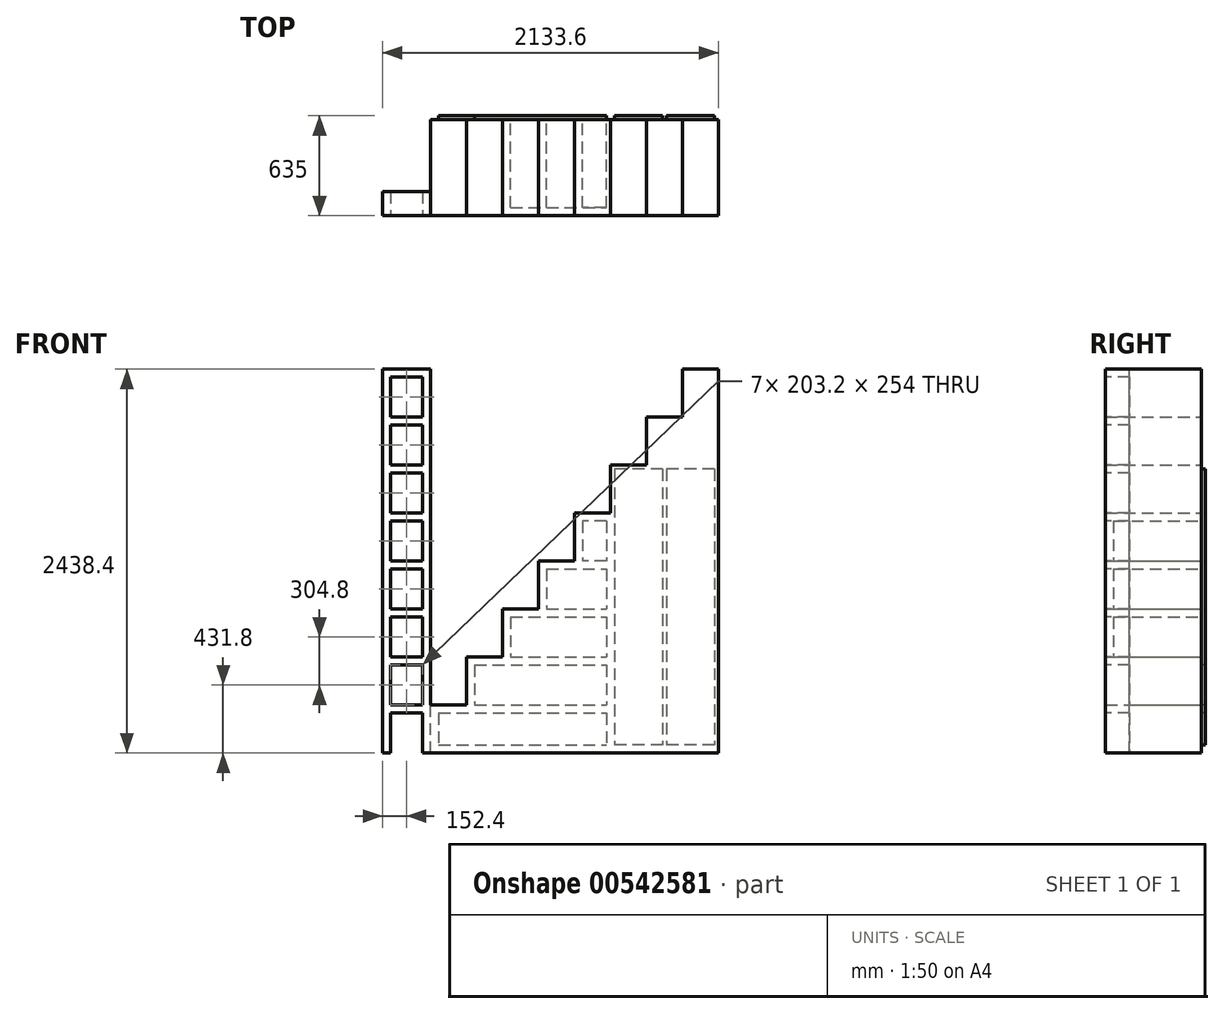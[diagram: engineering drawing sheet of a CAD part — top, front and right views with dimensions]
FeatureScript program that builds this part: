
annotation { "Feature Type Name" : "Feature", "Feature Type Description" : "" }
export const myFeature = defineFeature(function(context is Context, id is Id, definition is map)
    precondition{}
    {
        {
            var Q0;
            Q0=qCreatedBy(makeId("Front.planeOp"),FACE);
            var sketch = newSketch(context, id + "F0", { "sketchPlane" : qUnion([Q0])});
            skLineSegment(sketch, "E0.bottom", {"start": v(-1828.8, 0) * mm, "end": v(0, 0) * mm});
            skLineSegment(sketch, "E0.top", {"start": v(-1828.8, 304.8) * mm, "end": v(0, 304.8) * mm});
            skLineSegment(sketch, "E0.left", {"start": v(-1828.8, 0) * mm, "end": v(-1828.8, 304.8) * mm});
            skLineSegment(sketch, "E0.right", {"start": v(0, 0) * mm, "end": v(0, 304.8) * mm});
            skLineSegment(sketch, "E1.bottom", {"start": v(-1600.2, 304.8) * mm, "end": v(0, 304.8) * mm});
            skLineSegment(sketch, "E1.top", {"start": v(-1600.2, 609.6) * mm, "end": v(0, 609.6) * mm});
            skLineSegment(sketch, "E1.left", {"start": v(-1600.2, 304.8) * mm, "end": v(-1600.2, 609.6) * mm});
            skLineSegment(sketch, "E1.right", {"start": v(0, 304.8) * mm, "end": v(0, 609.6) * mm});
            skLineSegment(sketch, "E2.bottom", {"start": v(-1371.6, 609.6) * mm, "end": v(0, 609.6) * mm});
            skLineSegment(sketch, "E2.top", {"start": v(-1371.6, 914.4) * mm, "end": v(0, 914.4) * mm});
            skLineSegment(sketch, "E2.left", {"start": v(-1371.6, 609.6) * mm, "end": v(-1371.6, 914.4) * mm});
            skLineSegment(sketch, "E2.right", {"start": v(0, 609.6) * mm, "end": v(0, 914.4) * mm});
            skLineSegment(sketch, "E3.bottom", {"start": v(0, 914.4) * mm, "end": v(-1143, 914.4) * mm});
            skLineSegment(sketch, "E3.top", {"start": v(0, 1219.2) * mm, "end": v(-1143, 1219.2) * mm});
            skLineSegment(sketch, "E3.left", {"start": v(0, 914.4) * mm, "end": v(0, 1219.2) * mm});
            skLineSegment(sketch, "E3.right", {"start": v(-1143, 914.4) * mm, "end": v(-1143, 1219.2) * mm});
            skLineSegment(sketch, "E4.bottom", {"start": v(0, 1219.2) * mm, "end": v(-914.4, 1219.2) * mm});
            skLineSegment(sketch, "E4.top", {"start": v(0, 1524) * mm, "end": v(-914.4, 1524) * mm});
            skLineSegment(sketch, "E4.left", {"start": v(0, 1219.2) * mm, "end": v(0, 1524) * mm});
            skLineSegment(sketch, "E4.right", {"start": v(-914.4, 1219.2) * mm, "end": v(-914.4, 1524) * mm});
            skLineSegment(sketch, "E5.bottom", {"start": v(0, 1524) * mm, "end": v(-685.8, 1524) * mm});
            skLineSegment(sketch, "E5.top", {"start": v(0, 1828.8) * mm, "end": v(-685.8, 1828.8) * mm});
            skLineSegment(sketch, "E5.left", {"start": v(0, 1524) * mm, "end": v(0, 1828.8) * mm});
            skLineSegment(sketch, "E5.right", {"start": v(-685.8, 1524) * mm, "end": v(-685.8, 1828.8) * mm});
            skLineSegment(sketch, "E6.bottom", {"start": v(0, 1828.8) * mm, "end": v(-457.2, 1828.8) * mm});
            skLineSegment(sketch, "E6.top", {"start": v(0, 2133.6) * mm, "end": v(-457.2, 2133.6) * mm});
            skLineSegment(sketch, "E6.left", {"start": v(0, 1828.8) * mm, "end": v(0, 2133.6) * mm});
            skLineSegment(sketch, "E6.right", {"start": v(-457.2, 1828.8) * mm, "end": v(-457.2, 2133.6) * mm});
            skLineSegment(sketch, "E7.bottom", {"start": v(0, 2133.6) * mm, "end": v(-228.6, 2133.6) * mm});
            skLineSegment(sketch, "E7.top", {"start": v(0, 2438.4) * mm, "end": v(-228.6, 2438.4) * mm});
            skLineSegment(sketch, "E7.left", {"start": v(0, 2133.6) * mm, "end": v(0, 2438.4) * mm});
            skLineSegment(sketch, "E7.right", {"start": v(-228.6, 2133.6) * mm, "end": v(-228.6, 2438.4) * mm});
            skSolve(sketch);
        }
        {
            var Q0;
            Q0 = qSketchRegion(id + "F0", true);
            extrude(context, id + "F1", {"entities" : qUnion([Q0]), "depth" : 609.6 * mm, "offsetDistance" : 30.48 * mm});
        }
        {
            var Q0;
            Q0=makeQuery(id+"F1.opExtrude","CAP_FACE",FACE,{"disambiguationData":[OSD([sQuery(id+"F0.wireOp",EDGE,"E0.bottom"),sQuery(id+"F0.wireOp",EDGE,"E0.top"),sQuery(id+"F0.wireOp",EDGE,"E0.left"),sQuery(id+"F0.wireOp",EDGE,"E0.right"),sQuery(id+"F0.wireOp",EDGE,"E1.top"),sQuery(id+"F0.wireOp",EDGE,"E1.left"),sQuery(id+"F0.wireOp",EDGE,"E1.right"),sQuery(id+"F0.wireOp",EDGE,"E2.top"),sQuery(id+"F0.wireOp",EDGE,"E2.left"),sQuery(id+"F0.wireOp",EDGE,"E2.right"),sQuery(id+"F0.wireOp",EDGE,"E3.top"),sQuery(id+"F0.wireOp",EDGE,"E3.left"),sQuery(id+"F0.wireOp",EDGE,"E3.right"),sQuery(id+"F0.wireOp",EDGE,"E4.top"),sQuery(id+"F0.wireOp",EDGE,"E4.left"),sQuery(id+"F0.wireOp",EDGE,"E4.right"),sQuery(id+"F0.wireOp",EDGE,"E5.top"),sQuery(id+"F0.wireOp",EDGE,"E5.left"),sQuery(id+"F0.wireOp",EDGE,"E5.right"),sQuery(id+"F0.wireOp",EDGE,"E6.top"),sQuery(id+"F0.wireOp",EDGE,"E6.left"),sQuery(id+"F0.wireOp",EDGE,"E6.right"),sQuery(id+"F0.wireOp",EDGE,"E7.top"),sQuery(id+"F0.wireOp",EDGE,"E7.left"),sQuery(id+"F0.wireOp",EDGE,"E7.right")])],"isStart":false});
            var sketch = newSketch(context, id + "F2", { "sketchPlane" : qUnion([Q0])});
            skLineSegment(sketch, "E8.bottom", {"start": v(-1828.8, 0) * mm, "end": v(-1879.6, 0) * mm});
            skLineSegment(sketch, "E8.top", {"start": v(-1828.8, 2438.4) * mm, "end": v(-2133.6, 2438.4) * mm});
            skLineSegment(sketch, "E8.left", {"start": v(-1828.8, 0) * mm, "end": v(-1828.8, 2438.4) * mm});
            skLineSegment(sketch, "E8.right", {"start": v(-2133.6, 0) * mm, "end": v(-2133.6, 2438.4) * mm});
            skLineSegment(sketch, "E9.bottom", {"start": v(-2082.8, 2438.4) * mm, "end": v(-1879.6, 2438.4) * mm});
            skLineSegment(sketch, "E9.left", {"start": v(-2082.8, 2438.4) * mm, "end": v(-2082.8, 0) * mm});
            skLineSegment(sketch, "E9.right", {"start": v(-1879.6, 2438.4) * mm, "end": v(-1879.6, 0) * mm});
            skLineSegment(sketch, "E10", {"start": v(-1879.6, 304.8) * mm, "end": v(-2082.8, 304.8) * mm});
            skLineSegment(sketch, "E11", {"start": v(-1879.6, 609.6) * mm, "end": v(-2082.8, 609.6) * mm});
            skLineSegment(sketch, "E12", {"start": v(-1879.6, 914.4) * mm, "end": v(-2082.8, 914.4) * mm});
            skLineSegment(sketch, "E13", {"start": v(-1879.6, 863.6) * mm, "end": v(-2082.8, 863.6) * mm});
            skLineSegment(sketch, "E14", {"start": v(-2082.8, 558.8) * mm, "end": v(-1879.6, 558.8) * mm});
            skLineSegment(sketch, "E15", {"start": v(-2082.8, 254) * mm, "end": v(-1879.6, 254) * mm});
            skLineSegment(sketch, "E16.bottom", {"start": v(-2082.8, 1168.4) * mm, "end": v(-1879.6, 1168.4) * mm});
            skLineSegment(sketch, "E16.top", {"start": v(-2082.8, 1219.2) * mm, "end": v(-1879.6, 1219.2) * mm});
            skLineSegment(sketch, "E16.left", {"start": v(-2082.8, 1168.4) * mm, "end": v(-2082.8, 1219.2) * mm});
            skLineSegment(sketch, "E16.right", {"start": v(-1879.6, 1168.4) * mm, "end": v(-1879.6, 1219.2) * mm});
            skLineSegment(sketch, "E17.bottom", {"start": v(-1879.6, 1524) * mm, "end": v(-2082.8, 1524) * mm});
            skLineSegment(sketch, "E17.top", {"start": v(-1879.6, 1473.2) * mm, "end": v(-2082.8, 1473.2) * mm});
            skLineSegment(sketch, "E17.left", {"start": v(-1879.6, 1524) * mm, "end": v(-1879.6, 1473.2) * mm});
            skLineSegment(sketch, "E17.right", {"start": v(-2082.8, 1524) * mm, "end": v(-2082.8, 1473.2) * mm});
            skLineSegment(sketch, "E18.bottom", {"start": v(-1879.6, 1828.8) * mm, "end": v(-2082.8, 1828.8) * mm});
            skLineSegment(sketch, "E18.top", {"start": v(-1879.6, 1778) * mm, "end": v(-2082.8, 1778) * mm});
            skLineSegment(sketch, "E18.left", {"start": v(-1879.6, 1828.8) * mm, "end": v(-1879.6, 1778) * mm});
            skLineSegment(sketch, "E18.right", {"start": v(-2082.8, 1828.8) * mm, "end": v(-2082.8, 1778) * mm});
            skLineSegment(sketch, "E19.bottom", {"start": v(-1879.6, 2133.6) * mm, "end": v(-2082.8, 2133.6) * mm});
            skLineSegment(sketch, "E19.top", {"start": v(-1879.6, 2082.8) * mm, "end": v(-2082.8, 2082.8) * mm});
            skLineSegment(sketch, "E19.left", {"start": v(-1879.6, 2133.6) * mm, "end": v(-1879.6, 2082.8) * mm});
            skLineSegment(sketch, "E19.right", {"start": v(-2082.8, 2133.6) * mm, "end": v(-2082.8, 2082.8) * mm});
            skLineSegment(sketch, "E20.top", {"start": v(-1879.6, 2387.6) * mm, "end": v(-2082.8, 2387.6) * mm});
            skLineSegment(sketch, "E20.left", {"start": v(-1879.6, 2387.6) * mm, "end": v(-1879.6, 2340.42) * mm});
            skLineSegment(sketch, "E20.right", {"start": v(-2082.8, 2387.6) * mm, "end": v(-2082.8, 2340.42) * mm});
            skLineSegment(sketch, "E21.trimOffspring", {"start": v(-2082.8, 0) * mm, "end": v(-2133.6, 0) * mm});
            skSolve(sketch);
        }
        {
            var Q0;
            Q0 = qSketchRegion(id + "F2", true);
            var Q1;
            Q1=makeQuery(id+"F2.imprint","IMPRINT",FACE,{"disambiguationData":[TD([[makeQuery(id+"F2.imprint","IMPRINT",EDGE,{"derivedFrom":sQuery(id+"F2.wireOp",EDGE,"E19.bottom")}),1.0]])]});
            var Q2;
            Q2=makeQuery(id+"F2.imprint","IMPRINT",FACE,{"disambiguationData":[TD([[makeQuery(id+"F2.imprint","IMPRINT",EDGE,{"derivedFrom":sQuery(id+"F2.wireOp",EDGE,"E18.bottom")}),1.0]])]});
            var Q3;
            Q3=makeQuery(id+"F2.imprint","IMPRINT",FACE,{"disambiguationData":[TD([[makeQuery(id+"F2.imprint","IMPRINT",EDGE,{"derivedFrom":sQuery(id+"F2.wireOp",EDGE,"E17.bottom")}),1.0]])]});
            var Q4;
            Q4=makeQuery(id+"F2.imprint","IMPRINT",FACE,{"disambiguationData":[TD([[makeQuery(id+"F2.imprint","IMPRINT",EDGE,{"derivedFrom":sQuery(id+"F2.wireOp",EDGE,"E16.bottom")}),1.0]])]});
            var Q5;
            {var subQ0=sQuery(id+"F2.wireOp",EDGE,"E12");Q5=makeQuery(id+"F2.imprint","IMPRINT",FACE,{"disambiguationData":[TD([[makeQuery(id+"F2.imprint","IMPRINT",EDGE,{"derivedFrom":subQ0}),1.0]])]});}
            var Q6;
            {var subQ0=sQuery(id+"F2.wireOp",EDGE,"E11");Q6=makeQuery(id+"F2.imprint","IMPRINT",FACE,{"disambiguationData":[TD([[makeQuery(id+"F2.imprint","IMPRINT",EDGE,{"derivedFrom":subQ0}),1.0]])]});}
            extrude(context, id + "F3", {"entities" : qUnion([Q0, Q1, Q2, Q3, Q4, Q5, Q6]), "operationType" : NewBodyOperationType.ADD, "oppositeDirection" : true, "depth" : 152.4 * mm, "offsetDistance" : 25.4 * mm});
        }
        {
            var Q0;
            Q0=makeQuery(id+"F1.opExtrude","CAP_FACE",FACE,{"disambiguationData":[OSD([sQuery(id+"F0.wireOp",EDGE,"E0.bottom"),sQuery(id+"F0.wireOp",EDGE,"E0.top"),sQuery(id+"F0.wireOp",EDGE,"E0.left"),sQuery(id+"F0.wireOp",EDGE,"E0.right"),sQuery(id+"F0.wireOp",EDGE,"E1.top"),sQuery(id+"F0.wireOp",EDGE,"E1.left"),sQuery(id+"F0.wireOp",EDGE,"E1.right"),sQuery(id+"F0.wireOp",EDGE,"E2.top"),sQuery(id+"F0.wireOp",EDGE,"E2.left"),sQuery(id+"F0.wireOp",EDGE,"E2.right"),sQuery(id+"F0.wireOp",EDGE,"E3.top"),sQuery(id+"F0.wireOp",EDGE,"E3.left"),sQuery(id+"F0.wireOp",EDGE,"E3.right"),sQuery(id+"F0.wireOp",EDGE,"E4.top"),sQuery(id+"F0.wireOp",EDGE,"E4.left"),sQuery(id+"F0.wireOp",EDGE,"E4.right"),sQuery(id+"F0.wireOp",EDGE,"E5.top"),sQuery(id+"F0.wireOp",EDGE,"E5.left"),sQuery(id+"F0.wireOp",EDGE,"E5.right"),sQuery(id+"F0.wireOp",EDGE,"E6.top"),sQuery(id+"F0.wireOp",EDGE,"E6.left"),sQuery(id+"F0.wireOp",EDGE,"E6.right"),sQuery(id+"F0.wireOp",EDGE,"E7.top"),sQuery(id+"F0.wireOp",EDGE,"E7.left"),sQuery(id+"F0.wireOp",EDGE,"E7.right")])],"isStart":true});
            var sketch = newSketch(context, id + "F4", { "sketchPlane" : qUnion([Q0])});
            skLineSegment(sketch, "E22", {"start": v(0, 0) * mm, "end": v(1828.8, 0) * mm, "construction": true});
            skLineSegment(sketch, "E23", {"start": v(1828.8, 0) * mm, "end": v(1828.8, 304.8) * mm, "construction": true});
            skLineSegment(sketch, "E24", {"start": v(1828.8, 304.8) * mm, "end": v(1600.2, 304.8) * mm, "construction": true});
            skLineSegment(sketch, "E25", {"start": v(1600.2, 304.8) * mm, "end": v(1600.2, 609.6) * mm, "construction": true});
            skLineSegment(sketch, "E26", {"start": v(1600.2, 609.6) * mm, "end": v(1371.6, 609.6) * mm, "construction": true});
            skLineSegment(sketch, "E27", {"start": v(1371.6, 609.6) * mm, "end": v(1371.6, 914.4) * mm, "construction": true});
            skLineSegment(sketch, "E28", {"start": v(1371.6, 914.4) * mm, "end": v(1143, 914.4) * mm, "construction": true});
            skLineSegment(sketch, "E29", {"start": v(1143, 914.4) * mm, "end": v(1143, 1219.2) * mm, "construction": true});
            skLineSegment(sketch, "E30", {"start": v(1143, 1219.2) * mm, "end": v(914.4, 1219.2) * mm, "construction": true});
            skLineSegment(sketch, "E31", {"start": v(914.4, 1219.2) * mm, "end": v(914.4, 1524) * mm, "construction": true});
            skLineSegment(sketch, "E32", {"start": v(914.4, 1524) * mm, "end": v(685.8, 1524) * mm, "construction": true});
            skLineSegment(sketch, "E33", {"start": v(685.8, 1524) * mm, "end": v(685.8, 1828.8) * mm, "construction": true});
            skLineSegment(sketch, "E34", {"start": v(685.8, 1828.8) * mm, "end": v(457.2, 1828.8) * mm, "construction": true});
            skLineSegment(sketch, "E35", {"start": v(457.2, 1828.8) * mm, "end": v(457.2, 2133.6) * mm, "construction": true});
            skLineSegment(sketch, "E36", {"start": v(457.2, 2133.6) * mm, "end": v(228.6, 2133.6) * mm, "construction": true});
            skLineSegment(sketch, "E37", {"start": v(228.6, 2133.6) * mm, "end": v(228.6, 2438.4) * mm, "construction": true});
            skLineSegment(sketch, "E38", {"start": v(228.6, 2438.4) * mm, "end": v(0, 2438.4) * mm, "construction": true});
            skLineSegment(sketch, "E39", {"start": v(0, 2438.4) * mm, "end": v(0, 0) * mm, "construction": true});
            skLineSegment(sketch, "E40.bottom", {"start": v(25.4, 1803.4) * mm, "end": v(660.4, 1803.4) * mm});
            skLineSegment(sketch, "E40.top", {"start": v(25.4, 50.8) * mm, "end": v(660.4, 50.8) * mm});
            skLineSegment(sketch, "E40.left", {"start": v(25.4, 1803.4) * mm, "end": v(25.4, 50.8) * mm});
            skLineSegment(sketch, "E40.right", {"start": v(660.4, 1803.4) * mm, "end": v(660.4, 50.8) * mm});
            skLineSegment(sketch, "E41.bottom", {"start": v(711.2, 1473.2) * mm, "end": v(863.6, 1473.2) * mm});
            skLineSegment(sketch, "E41.top", {"start": v(711.2, 1219.2) * mm, "end": v(863.6, 1219.2) * mm});
            skLineSegment(sketch, "E41.left", {"start": v(711.2, 1473.2) * mm, "end": v(711.2, 1219.2) * mm});
            skLineSegment(sketch, "E41.right", {"start": v(863.6, 1473.2) * mm, "end": v(863.6, 1219.2) * mm});
            skLineSegment(sketch, "E42.bottom", {"start": v(1092.2, 1168.4) * mm, "end": v(711.2, 1168.4) * mm});
            skLineSegment(sketch, "E42.top", {"start": v(1092.2, 914.4) * mm, "end": v(711.2, 914.4) * mm});
            skLineSegment(sketch, "E42.left", {"start": v(1092.2, 1168.4) * mm, "end": v(1092.2, 914.4) * mm});
            skLineSegment(sketch, "E42.right", {"start": v(711.2, 1168.4) * mm, "end": v(711.2, 914.4) * mm});
            skLineSegment(sketch, "E43.bottom", {"start": v(1320.8, 863.6) * mm, "end": v(711.2, 863.6) * mm});
            skLineSegment(sketch, "E43.top", {"start": v(1320.8, 609.6) * mm, "end": v(711.2, 609.6) * mm});
            skLineSegment(sketch, "E43.left", {"start": v(1320.8, 863.6) * mm, "end": v(1320.8, 609.6) * mm});
            skLineSegment(sketch, "E43.right", {"start": v(711.2, 863.6) * mm, "end": v(711.2, 609.6) * mm});
            skLineSegment(sketch, "E44.bottom", {"start": v(1549.4, 558.8) * mm, "end": v(711.2, 558.8) * mm});
            skLineSegment(sketch, "E44.top", {"start": v(1549.4, 304.8) * mm, "end": v(711.2, 304.8) * mm});
            skLineSegment(sketch, "E44.left", {"start": v(1549.4, 558.8) * mm, "end": v(1549.4, 304.8) * mm});
            skLineSegment(sketch, "E44.right", {"start": v(711.2, 558.8) * mm, "end": v(711.2, 304.8) * mm});
            skLineSegment(sketch, "E45.bottom", {"start": v(1778, 254) * mm, "end": v(711.2, 254) * mm});
            skLineSegment(sketch, "E45.top", {"start": v(1778, 50.8) * mm, "end": v(711.2, 50.8) * mm});
            skLineSegment(sketch, "E45.left", {"start": v(1778, 254) * mm, "end": v(1778, 50.8) * mm});
            skLineSegment(sketch, "E45.right", {"start": v(711.2, 254) * mm, "end": v(711.2, 50.8) * mm});
            skLineSegment(sketch, "E46.bottom", {"start": v(330.2, 1803.4) * mm, "end": v(355.6, 1803.4) * mm});
            skLineSegment(sketch, "E46.top", {"start": v(330.2, 50.8) * mm, "end": v(355.6, 50.8) * mm});
            skLineSegment(sketch, "E46.left", {"start": v(330.2, 1803.4) * mm, "end": v(330.2, 50.8) * mm});
            skLineSegment(sketch, "E46.right", {"start": v(355.6, 1803.4) * mm, "end": v(355.6, 50.8) * mm});
            skSolve(sketch);
        }
        {
            var Q0;
            Q0=makeQuery(id+"F4.imprint","IMPRINT",FACE,{"disambiguationData":[TD([[makeQuery(id+"F4.imprint","IMPRINT",EDGE,{"derivedFrom":sQuery(id+"F4.wireOp",EDGE,"E41.bottom")}),-1.0]])]});
            var Q1;
            Q1=makeQuery(id+"F4.imprint","IMPRINT",FACE,{"disambiguationData":[TD([[makeQuery(id+"F4.imprint","IMPRINT",EDGE,{"derivedFrom":sQuery(id+"F4.wireOp",EDGE,"E42.bottom")}),1.0]])]});
            var Q2;
            Q2=makeQuery(id+"F4.imprint","IMPRINT",FACE,{"disambiguationData":[TD([[makeQuery(id+"F4.imprint","IMPRINT",EDGE,{"derivedFrom":sQuery(id+"F4.wireOp",EDGE,"E43.bottom")}),1.0]])]});
            extrude(context, id + "F5", {"entities" : qUnion([Q0, Q1, Q2]), "operationType" : NewBodyOperationType.REMOVE, "oppositeDirection" : true, "depth" : 558.8 * mm, "offsetDistance" : 25.4 * mm});
        }
        {
            var Q0;
            {var subQ0=sQuery(id+"F4.wireOp",EDGE,"E40.left");Q0=makeQuery(id+"F4.imprint","IMPRINT",FACE,{"disambiguationData":[TD([[makeQuery(id+"F4.imprint","IMPRINT",EDGE,{"derivedFrom":subQ0}),1.0]])]});}
            var Q1;
            {var subQ0=sQuery(id+"F4.wireOp",EDGE,"E40.right");Q1=makeQuery(id+"F4.imprint","IMPRINT",FACE,{"disambiguationData":[TD([[makeQuery(id+"F4.imprint","IMPRINT",EDGE,{"derivedFrom":subQ0}),-1.0]])]});}
            var Q2;
            Q2=makeQuery(id+"F4.imprint","IMPRINT",FACE,{"disambiguationData":[TD([[makeQuery(id+"F4.imprint","IMPRINT",EDGE,{"derivedFrom":sQuery(id+"F4.wireOp",EDGE,"E44.bottom")}),1.0]])]});
            var Q3;
            Q3=makeQuery(id+"F4.imprint","IMPRINT",FACE,{"disambiguationData":[TD([[makeQuery(id+"F4.imprint","IMPRINT",EDGE,{"derivedFrom":sQuery(id+"F4.wireOp",EDGE,"E45.bottom")}),1.0]])]});
            extrude(context, id + "F6", {"entities" : qUnion([Q0, Q1, Q2, Q3]), "operationType" : NewBodyOperationType.ADD, "depth" : 25.4 * mm, "offsetDistance" : 25.4 * mm});
        }
    });
